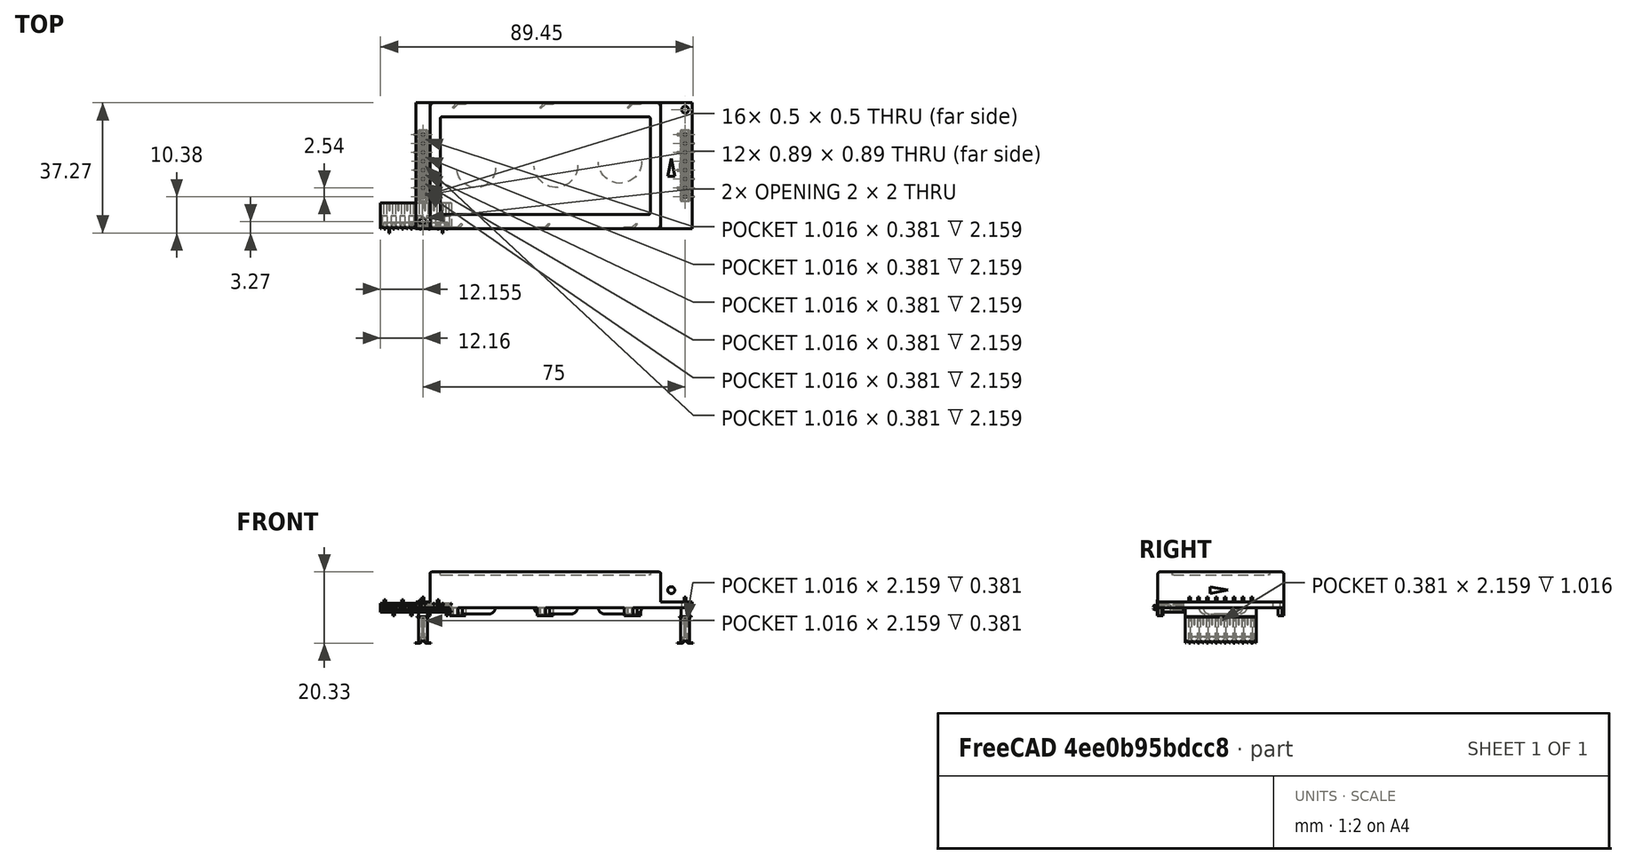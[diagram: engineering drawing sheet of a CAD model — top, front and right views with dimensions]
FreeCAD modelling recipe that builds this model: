
FCSTD DOCUMENT  (FreeCAD 0.18R4 (GitTag))
Label: Display with header
License: All rights reserved
LicenseURL: http://en.wikipedia.org/wiki/All_rights_reserved
objects: Part::Feature×9, Part::Compound×2, App::Part×2, Part::Cone×1
note: 12 computed .brp shape members not serialized (recipe doc carries the construction recipe); baked Part::Feature solids carry a one-line shape summary decoded from their .brp

FEATURE [Part::Feature] NHD_0420H1Z
  shape: bbox 79 x 36 x 18.74 mm, 242 faces (baked)
FEATURE [Part::Feature] SSM_108_S_SV_K_TR
  shape: bbox 20.32 x 7.493 x 3.505 mm, 213 faces (baked)
FEATURE [Part::Feature] SSM_108_S_SV_K_TR001
  Placement = pos=(0,-0.127,0) rot=(0,0,1;0rad)
  shape: bbox 18.29 x 1.905 x 4.572 mm, 92 faces (baked)
FEATURE [Part::Compound] Compound
  Links = -> [SSM_108_S_SV_K_TR,SSM_108_S_SV_K_TR001]
  Placement = pos=(77,18,-10) rot=(0.57735,0.57735,0.57735;2.0944rad)
FEATURE [Part::Feature] SSM_108_S_SV_K_TR002
  shape: bbox 20.32 x 7.493 x 3.505 mm, 213 faces (baked)
FEATURE [Part::Feature] SSM_108_S_SV_K_TR003
  Placement = pos=(0,-0.127,0) rot=(0,0,1;0rad)
  shape: bbox 18.29 x 1.905 x 4.572 mm, 92 faces (baked)
FEATURE [Part::Compound] Compound001
  Links = -> [SSM_108_S_SV_K_TR002,SSM_108_S_SV_K_TR003]
  Placement = pos=(2,18,-10) rot=(0.57735,0.57735,0.57735;2.0944rad)
FEATURE [Part::Cone] Cone
  Angle = 360
  AttacherType = Attacher::AttachEngine3D
  Height = 5
  Placement = pos=(73,20,5) rot=(1,0,0;1.5708rad)
  Radius1 = 0
  Radius2 = 1
FEATURE [Part::Feature] Part__Feature  label="_SSM-108-L-SV-BE-LC_body"
  shape: bbox 20.32 x 8.636 x 2.54 mm, 291 faces (baked)
FEATURE [Part::Feature] Part__Feature001  label="_C-95-028"
  Placement = pos=(0,-0.127,0) rot=(0,0,1;0rad)
  shape: bbox 18.29 x 1.905 x 4.572 mm, 92 faces (baked)
FEATURE [App::Part] SSM_108_L_SV_BE_LC  label="SSM-108-L-SV-BE-LC"
  Group = -> [Part__Feature,Part__Feature001]
  Origin = -> Origin
  Placement = pos=(2,18,-10) rot=(0.57735,0.57735,0.57735;2.0944rad)
FEATURE [Part::Feature] Part__Feature002  label="_SSM-108-L-SV-BE-LC_body001"
  shape: bbox 20.32 x 8.636 x 2.54 mm, 291 faces (baked)
FEATURE [Part::Feature] Part__Feature003  label="_C-95-029"
  Placement = pos=(0,-0.127,0) rot=(0,0,1;0rad)
  shape: bbox 18.29 x 1.905 x 4.572 mm, 92 faces (baked)
FEATURE [App::Part] SSM_108_L_SV_BE_LC001  label="SSM-108-L-SV-BE-LC001"
  Group = -> [Part__Feature002,Part__Feature003]
  Origin = -> Origin001
  Placement = pos=(77,18,-10) rot=(0.57735,0.57735,0.57735;2.0944rad)
